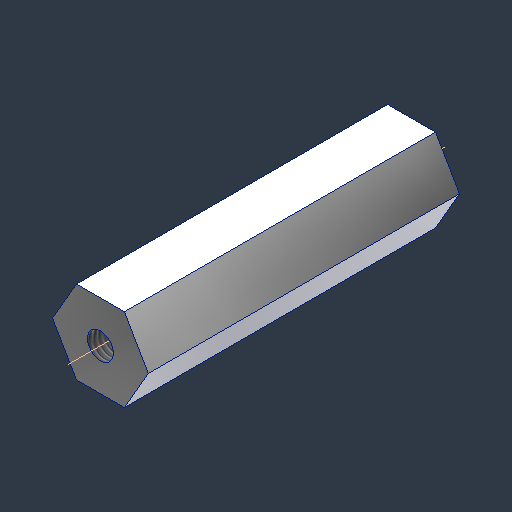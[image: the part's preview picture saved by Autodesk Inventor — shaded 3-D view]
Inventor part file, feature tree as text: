
AUTODESK INVENTOR PART (.ipt)
format: ipt  version: 2024.3 (Build 283343000, 343)  size: 105,472 bytes
history: native  units: mm (DEFAULTED — no unit token found)
features: sketch x2, extrude x1, hole x1
ambient origin geometry x8: Origin, YZ Plane, XZ Plane, XY Plane, X Axis, Y Axis, Z Axis, Center Point
bodies: Solid1 (feature_tree)
feature tree (4):
  extrude  "Extrusion1"  Depth=47.625mm TaperAngle=0.0deg
  hole  "Hole1"  [1 undecoded]
  sketch  "Sketch2"  dims[d0=12.7mm d1=47.625mm d2=0.0mm]
  sketch  "Sketch3"  dims[d3=3.9624mm d4=9.652mm d5=9.525mm d6=4.826mm d7=14.3117mm d8=25.4mm d9=20.594885mm]
note: 1 required parameter value undecoded (feature->parameter linkage not recoverable at this tier; creation-order binding heuristic only, values carry confidence <= 0.55)
